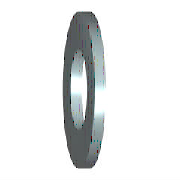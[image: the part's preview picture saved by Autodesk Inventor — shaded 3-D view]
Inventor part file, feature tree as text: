
AUTODESK INVENTOR PART (.ipt)
format: ipt  version: 2025 (Build 290162010, 162A)  size: 108,032 bytes
history: native  units: mm (DEFAULTED — no unit token found)
features: other x1, plane x1
ambient origin geometry x7: Origin, YZ Plane, XY Plane, X Axis, Y Axis, Z Axis, Center Point
bodies: Solid1 (feature_tree), Body (feature_tree)
feature tree (2):
  other  "Work Axis1"
  plane  "Work Plane1"
